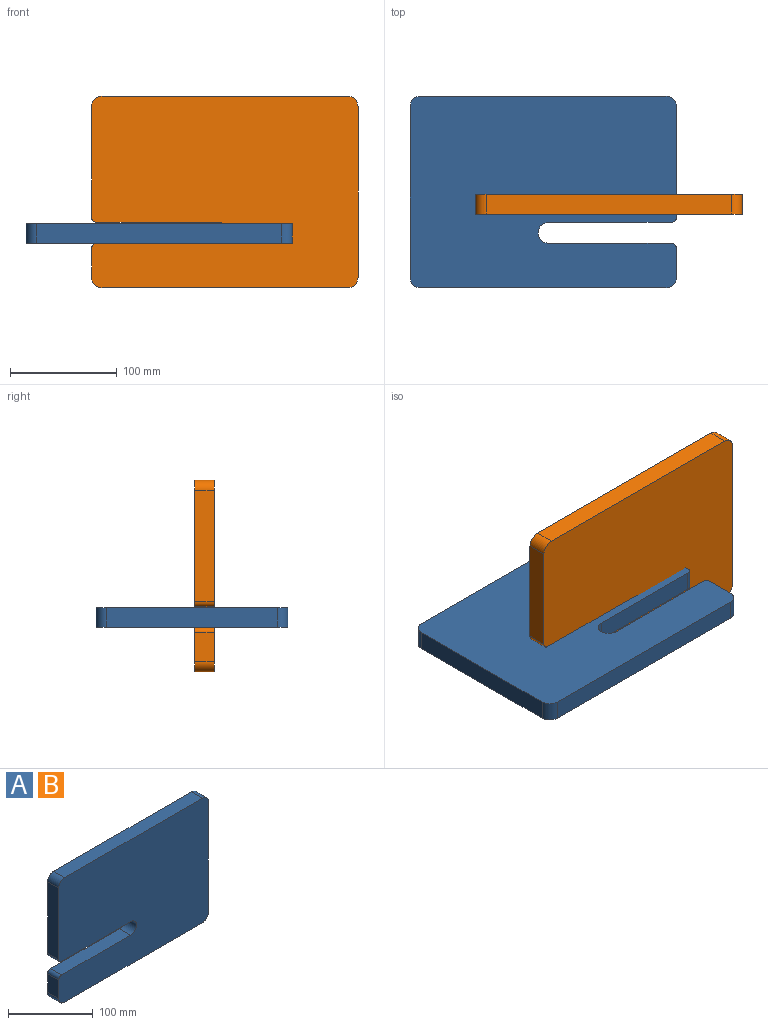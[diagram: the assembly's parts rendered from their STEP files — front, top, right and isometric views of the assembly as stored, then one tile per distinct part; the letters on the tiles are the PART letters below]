
ASSEMBLY  parts=2 mates=2
PART A: 16 faces, bbox 250x18.5x180 mm
  f0: plane 26.92x18.5mm, normal (-1,0,0), area 498mm2, adj f1,f6,f9,f15
  f1: plane 250x180mm, normal (0,-1,0), area 42414.1mm2, adj f0,f2,f3,f4,f5,f7,f8,f9
  f2: plane 160x18.5mm, normal (1,0,0), area 2960mm2, adj f1,f6,f7,f10
  f3: plane 230x18.5mm, normal (0,0,1), area 4255mm2, adj f1,f6,f7,f8
  f4: plane 103.58x18.5mm, normal (-1,0,0), area 1916.3mm2, adj f1,f6,f8,f14
  f5: plane 230x18.5mm, normal (0,0,-1), area 4255mm2, adj f1,f6,f9,f10
  f6: plane 250x180mm, normal (0,1,0), area 42414.1mm2, adj f0,f2,f3,f4,f5,f7,f8,f9
  f7: cylinder r=10mm len=18.5mm, axis (0,-1,0), area 290.6mm2, adj f1,f2,f3,f6
  f8: cylinder r=10mm len=18.5mm, axis (0,1,0), area 290.6mm2, adj f1,f3,f4,f6
  f9: cylinder r=10mm len=18.5mm, axis (0,-1,0), area 290.6mm2, adj f0,f1,f5,f6
  f10: cylinder r=10mm len=18.5mm, axis (0,1,0), area 290.6mm2, adj f1,f2,f5,f6
  f11: cylinder r=9.75mm len=19.5mm, axis (0,-1,0), area 566.7mm2, adj f1,f6,f12,f13
  f12: plane 115x18.5mm, normal (0,0,1), area 2127.5mm2, adj f1,f6,f11,f15
  f13: plane 115x18.5mm, normal (0,0,-1), area 2127.5mm2, adj f1,f6,f11,f14
  f14: cylinder r=5mm len=18.5mm, axis (0,1,0), area 145.3mm2, adj f1,f4,f6,f13
  f15: cylinder r=5mm len=18.5mm, axis (0,-1,0), area 145.3mm2, adj f0,f1,f6,f12
PART B: same geometry as A
PLACE A rot(axis=(0,0.71,0.71),180deg) t=(44.62,75.18,16.44)mm
PLACE B t=(106.13,72.78,46.02)mm
MATE parallel A.f5 <-> B.f1  axis (0,-1,0) through (44.62,-14.82,7.19)mm
MATE planar A.f1 <-> B.f12  axis (0,0,-1) through (41,77.44,-2.06)mm
